SOLIDWORKS PART (.sldprt)
format: sldprt  version: not decoded by parser v0  size: 201,216 bytes
history: native  units: mm
features: sketch x4, extrude x2, material x1, cut_revolve x1, cut_extrude x1 (+14 scaffold rows collapsed)
feature tree (23):
  scaffold x14  (default folders/planes/origin — collapsed)
  material  "AISI 316 Annealed Stainless Steel Bar (SS)"
  sketch  "Sketch1"  dims[MM=7.9248mm]
  extrude  "Extrude1"  [1 undecoded]
  sketch  "Sketch2"  dims[Bore=26.9875mm]
  extrude  "Piston"  Depth=5mm
  sketch  "Sketch3"  dims[c1.KK=7.92mm c1.D1=~1.806723mm c2.D1=45.0deg c2.D2=0.5mm c2.D3=2.0mm c2.A=12.7mm c2.D4=0.5mm]
  cut_revolve  "Threads"  Angle=360deg
  sketch  "Sketch4"  dims[D=6.35mm K=3.048mm]
  cut_extrude  "Flats"  [1 undecoded]
decode coverage: 6 of 8 modeling features carry decoded parameters
note: ~ marks probable driven/reference dimensions
note: 2 parameter values undecoded
note: suppression state not decoded; provenance and decode notes live in map.json
